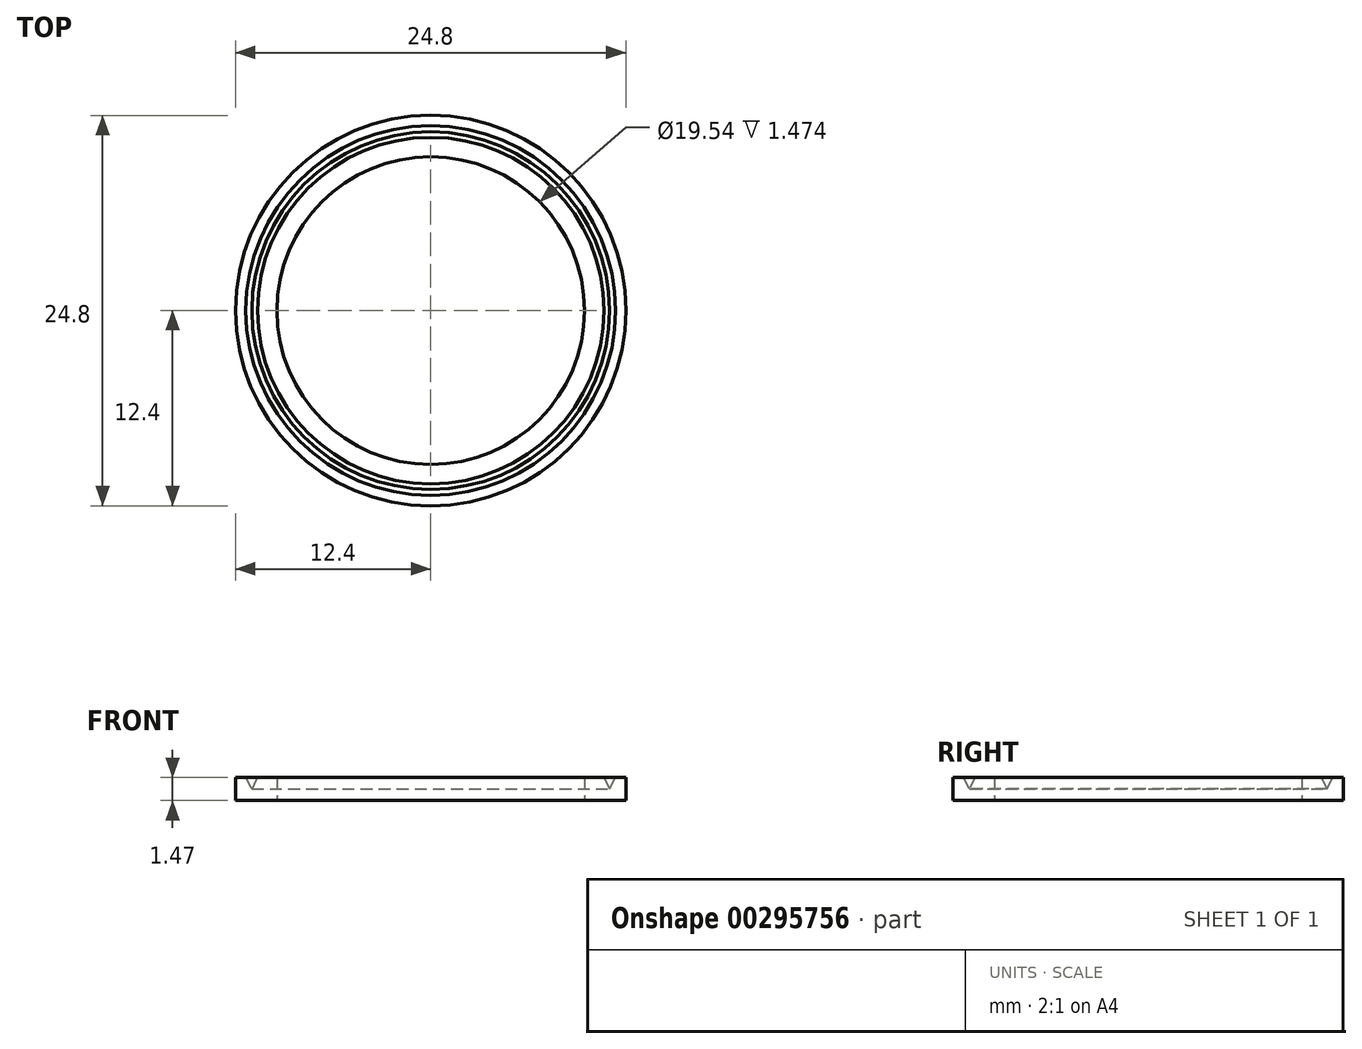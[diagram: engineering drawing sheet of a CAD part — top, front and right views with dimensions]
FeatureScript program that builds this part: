
annotation { "Feature Type Name" : "Feature", "Feature Type Description" : "" }
export const myFeature = defineFeature(function(context is Context, id is Id, definition is map)
    precondition{}
    {
        {
            var Q0;
            Q0=qCreatedBy(makeId("Front.planeOp"),FACE);
            var sketch = newSketch(context, id + "F0", { "sketchPlane" : qUnion([Q0])});
            skLineSegment(sketch, "E0", {"start": v(0, 0) * mm, "end": v(0, 5.32) * mm, "construction": true});
            skLineSegment(sketch, "E1.bottom", {"start": v(9.77, -3.24) * mm, "end": v(12.4, -3.24) * mm});
            skLineSegment(sketch, "E1.top", {"start": v(9.77, -4.7) * mm, "end": v(12.4, -4.7) * mm});
            skLineSegment(sketch, "E1.left", {"start": v(9.77, -3.24) * mm, "end": v(9.77, -4.7) * mm});
            skLineSegment(sketch, "E1.right", {"start": v(12.4, -3.24) * mm, "end": v(12.4, -4.7) * mm});
            skLineSegment(sketch, "E2", {"start": v(7.07, -13.6) * mm, "end": v(23.35, -1.15) * mm, "construction": true});
            skLineSegment(sketch, "E3", {"start": v(-1.28, -13.1) * mm, "end": v(-12, 0) * mm, "construction": true});
            skSolve(sketch);
        }
        {
            var Q0;
            Q0 = qSketchRegion(id + "F0", true);
            var Q1;
            Q1=sQuery(id+"F0.wireOp",EDGE,"E0");
            revolve(context, id + "F1", {"entities" : qUnion([Q0]), "axis" : qUnion([Q1]), "revolveType" : RevolveType.FULL});
        }
        {
            var Q0;
            Q0=qCreatedBy(makeId("Front.planeOp"),FACE);
            var sketch = newSketch(context, id + "F2", { "sketchPlane" : qUnion([Q0])});
            skLineSegment(sketch, "E4", {"start": v(-12.34, -2.12) * mm, "end": v(-11.36, -3.96) * mm});
            skLineSegment(sketch, "E5", {"start": v(-11.36, -3.96) * mm, "end": v(-10.46, -2.12) * mm});
            skLineSegment(sketch, "E6", {"start": v(-10.46, -2.12) * mm, "end": v(-12.34, -2.12) * mm});
            skSolve(sketch);
        }
        {
            var Q0;
            Q0 = qSketchRegion(id + "F2", true);
            var Q1;
            Q1=sQuery(id+"F0.wireOp",EDGE,"E0");
            revolve(context, id + "F3", {"operationType" : NewBodyOperationType.REMOVE, "entities" : qUnion([Q0]), "axis" : qUnion([Q1]), "revolveType" : RevolveType.FULL});
        }
    });
